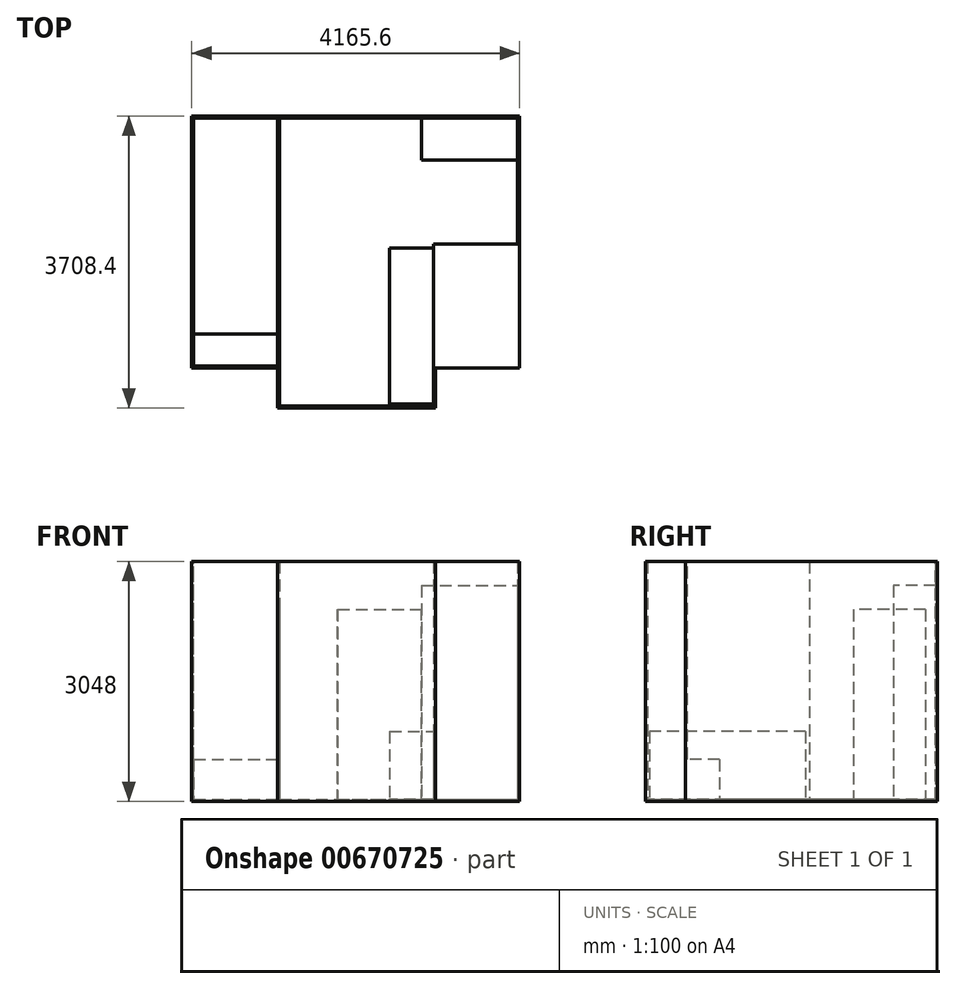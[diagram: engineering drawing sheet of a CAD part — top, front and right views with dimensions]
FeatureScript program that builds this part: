
annotation { "Feature Type Name" : "Feature", "Feature Type Description" : "" }
export const myFeature = defineFeature(function(context is Context, id is Id, definition is map)
    precondition{}
    {
        {
            var Q0;
            Q0=qCreatedBy(makeId("Top.planeOp"),FACE);
            var sketch = newSketch(context, id + "F0", { "sketchPlane" : qUnion([Q0])});
            skLineSegment(sketch, "E0.bottom", {"start": v(0, 0) * mm, "end": v(4165.6, 0) * mm});
            skLineSegment(sketch, "E0.top", {"start": v(1092.2, -3708.4) * mm, "end": v(3098.8, -3708.4) * mm});
            skLineSegment(sketch, "E0.left", {"start": v(0, 0) * mm, "end": v(0, -3200.4) * mm});
            skLineSegment(sketch, "E0.right", {"start": v(4165.6, 0) * mm, "end": v(4165.6, -3200.4) * mm});
            skLineSegment(sketch, "E1", {"start": v(0, -3200.4) * mm, "end": v(1092.2, -3200.4) * mm});
            skLineSegment(sketch, "E2", {"start": v(1092.2, -3200.4) * mm, "end": v(1092.2, -3708.4) * mm});
            skLineSegment(sketch, "E3", {"start": v(4165.6, -3200.4) * mm, "end": v(3098.8, -3200.4) * mm});
            skLineSegment(sketch, "E4", {"start": v(3098.8, -3200.4) * mm, "end": v(3098.8, -3708.4) * mm});
            skSolve(sketch);
        }
        {
            var Q0;
            Q0=makeQuery(id+"F0.imprint","IMPRINT",FACE,{"disambiguationData":[TD([[makeQuery(id+"F0.imprint","IMPRINT",EDGE,{"derivedFrom":sQuery(id+"F0.wireOp",EDGE,"E0.bottom")}),-1.0]])]});
            var sketch = newSketch(context, id + "F1", { "sketchPlane" : qUnion([Q0])});
            skLineSegment(sketch, "E5.bottom", {"start": v(0, -3200.4) * mm, "end": v(1117.6, -3200.4) * mm});
            skLineSegment(sketch, "E5.top", {"start": v(0, 0) * mm, "end": v(1117.6, 0) * mm});
            skLineSegment(sketch, "E5.left", {"start": v(0, -3200.4) * mm, "end": v(0, 0) * mm});
            skLineSegment(sketch, "E6", {"start": v(1117.6, 0) * mm, "end": v(1117.6, -3200.4) * mm});
            skSolve(sketch);
        }
        {
            var Q0;
            Q0=makeQuery(id+"F0.imprint","IMPRINT",FACE,{"disambiguationData":[TD([[makeQuery(id+"F0.imprint","IMPRINT",EDGE,{"derivedFrom":sQuery(id+"F0.wireOp",EDGE,"E0.bottom")}),-1.0]])]});
            var sketch = newSketch(context, id + "F2", { "sketchPlane" : qUnion([Q0])});
            skLineSegment(sketch, "E7.bottom", {"start": v(4165.6, -3200.4) * mm, "end": v(3073.4, -3200.4) * mm});
            skLineSegment(sketch, "E7.top", {"start": v(4165.6, -1625.6) * mm, "end": v(3073.4, -1625.6) * mm});
            skLineSegment(sketch, "E7.left", {"start": v(4165.6, -3200.4) * mm, "end": v(4165.6, -1625.6) * mm});
            skLineSegment(sketch, "E7.right", {"start": v(3073.4, -3200.4) * mm, "end": v(3073.4, -1625.6) * mm});
            skSolve(sketch);
        }
        {
            var Q0;
            Q0=makeQuery(id+"F0.imprint","IMPRINT",FACE,{"disambiguationData":[TD([[makeQuery(id+"F0.imprint","IMPRINT",EDGE,{"derivedFrom":sQuery(id+"F0.wireOp",EDGE,"E0.bottom")}),-1.0]])]});
            var sketch = newSketch(context, id + "F3", { "sketchPlane" : qUnion([Q0])});
            skLineSegment(sketch, "E8.bottom", {"start": v(4165.6, 0) * mm, "end": v(2921, 0) * mm});
            skLineSegment(sketch, "E8.top", {"start": v(4165.6, -558.8) * mm, "end": v(2921, -558.8) * mm});
            skLineSegment(sketch, "E8.left", {"start": v(4165.6, 0) * mm, "end": v(4165.6, -558.8) * mm});
            skLineSegment(sketch, "E8.right", {"start": v(2921, 0) * mm, "end": v(2921, -558.8) * mm});
            skSolve(sketch);
        }
        {
            var Q0;
            Q0=qCreatedBy(makeId("Top.planeOp"),FACE);
            var sketch = newSketch(context, id + "F4", { "sketchPlane" : qUnion([Q0])});
            skLineSegment(sketch, "E9.bottom", {"start": v(2514.6, -1676.4) * mm, "end": v(3073.4, -1676.4) * mm});
            skLineSegment(sketch, "E9.top", {"start": v(2514.6, -3657.6) * mm, "end": v(3073.4, -3657.6) * mm});
            skLineSegment(sketch, "E9.left", {"start": v(2514.6, -1676.4) * mm, "end": v(2514.6, -3657.6) * mm});
            skLineSegment(sketch, "E9.right", {"start": v(3073.4, -1676.4) * mm, "end": v(3073.4, -3657.6) * mm});
            skSolve(sketch);
        }
        {
            var Q0;
            Q0 = qSketchRegion(id + "F0", true);
            extrude(context, id + "F5", {"entities" : qUnion([Q0]), "depth" : 3048 * mm, "offsetDistance" : 25.4 * mm});
        }
        {
            var Q0;
            Q0=makeQuery(id+"F5.opExtrude","SWEPT_FACE",FACE,{"disambiguationData":[OSD([sQuery(id+"F0.wireOp",EDGE,"E0.bottom")])]});
            var sketch = newSketch(context, id + "F6", { "sketchPlane" : qUnion([Q0])});
            skLineSegment(sketch, "E10.bottom", {"start": v(-2921, 0) * mm, "end": v(-1854.2, 0) * mm});
            skLineSegment(sketch, "E10.top", {"start": v(-2921, 2438.4) * mm, "end": v(-1854.2, 2438.4) * mm});
            skLineSegment(sketch, "E10.left", {"start": v(-2921, 0) * mm, "end": v(-2921, 2438.4) * mm});
            skLineSegment(sketch, "E10.right", {"start": v(-1854.2, 0) * mm, "end": v(-1854.2, 2438.4) * mm});
            skSolve(sketch);
        }
        {
            var Q0;
            Q0=makeQuery(id+"F5.opExtrude","CAP_FACE",FACE,{"disambiguationData":[OSD([sQuery(id+"F0.wireOp",EDGE,"E0.bottom"),sQuery(id+"F0.wireOp",EDGE,"E0.top"),sQuery(id+"F0.wireOp",EDGE,"E0.left"),sQuery(id+"F0.wireOp",EDGE,"E0.right"),sQuery(id+"F0.wireOp",EDGE,"E1"),sQuery(id+"F0.wireOp",EDGE,"E2"),sQuery(id+"F0.wireOp",EDGE,"E3"),sQuery(id+"F0.wireOp",EDGE,"E4")])],"isStart":false});
            shell(context, id + "F7", {"entities" : qUnion([Q0]), "thickness" : 25.4 * mm});
        }
        {
            var Q0;
            Q0=makeQuery(id+"F6.imprint","IMPRINT",FACE,{"disambiguationData":[TD([[makeQuery(id+"F6.imprint","IMPRINT",EDGE,{"derivedFrom":sQuery(id+"F6.wireOp",EDGE,"E10.bottom")}),-1.0]])]});
            var Q1;
            Q1=makeQuery(id+"F7.opShell","OFFSET_FACE",FACE,{"disambiguationData":[OSD([sQuery(id+"F0.wireOp",EDGE,"E0.bottom")])]});
            extrude(context, id + "F8", {"entities" : qUnion([Q0]), "operationType" : NewBodyOperationType.REMOVE, "endBound" : BoundingType.UP_TO_SURFACE, "oppositeDirection" : true, "depth" : 25.4 * mm, "endBoundEntityFace" : qUnion([Q1]), "offsetDistance" : 25.4 * mm});
        }
        {
            var Q0;
            Q0 = qSketchRegion(id + "F1", true);
            extrude(context, id + "F9", {"entities" : qUnion([Q0]), "operationType" : NewBodyOperationType.ADD, "depth" : 3048 * mm, "offsetDistance" : 25.4 * mm});
        }
        {
            var Q0;
            Q0 = qSketchRegion(id + "F2", true);
            extrude(context, id + "F10", {"entities" : qUnion([Q0]), "operationType" : NewBodyOperationType.ADD, "depth" : 3048 * mm, "offsetDistance" : 25.4 * mm});
        }
        {
            var Q0;
            Q0 = qSketchRegion(id + "F4", true);
            extrude(context, id + "F11", {"entities" : qUnion([Q0]), "operationType" : NewBodyOperationType.ADD, "depth" : 889 * mm, "offsetDistance" : 25.4 * mm});
        }
        {
            var Q0;
            Q0 = qSketchRegion(id + "F3", true);
            extrude(context, id + "F12", {"entities" : qUnion([Q0]), "operationType" : NewBodyOperationType.ADD, "depth" : 508 * mm, "offsetDistance" : 25.4 * mm});
        }
        {
            var Q0;
            {var subQ0=sQuery(id+"F3.wireOp",EDGE,"E8.top");var subQ1=sQuery(id+"F3.wireOp",EDGE,"E8.right");Q0=makeQuery(id+"F12.boolean.opBoolean","SPLIT",FACE,{"disambiguationData":[TD([makeQuery(id+"F7.opShell","OFFSET_FACE",FACE,{"disambiguationData":[OSD([sQuery(id+"F0.wireOp",EDGE,"E0.bottom")])]})])],"derivedFrom":makeQuery(id+"F12.opExtrude","CAP_FACE",FACE,{"disambiguationData":[OSD([sQuery(id+"F3.wireOp",EDGE,"E8.bottom"),subQ0,sQuery(id+"F3.wireOp",EDGE,"E8.left"),subQ1])],"isStart":false})});}
            var sketch = newSketch(context, id + "F13", { "sketchPlane" : qUnion([Q0])});
            skLineSegment(sketch, "E11.bottom", {"start": v(4140.2, -558.8) * mm, "end": v(2921, -558.8) * mm});
            skLineSegment(sketch, "E11.top", {"start": v(4140.2, -25.4) * mm, "end": v(2921, -25.4) * mm});
            skLineSegment(sketch, "E11.left", {"start": v(4140.2, -558.8) * mm, "end": v(4140.2, -25.4) * mm});
            skLineSegment(sketch, "E11.right", {"start": v(2921, -558.8) * mm, "end": v(2921, -25.4) * mm});
            skSolve(sketch);
        }
        {
            var Q0;
            Q0 = qSketchRegion(id + "F13", true);
            extrude(context, id + "F14", {"entities" : qUnion([Q0]), "operationType" : NewBodyOperationType.ADD, "depth" : 2235.2 * mm, "offsetDistance" : 25.4 * mm});
        }
        {
            var Q0;
            Q0=makeQuery(id+"F9.boolean.opBoolean","MERGE",FACE,{"derivedFrom":[makeQuery(id+"F7.opShell","OFFSET_FACE",FACE,{"disambiguationData":[OSD([sQuery(id+"F0.wireOp",EDGE,"E2")])]}),makeQuery(id+"F9.opExtrude","SWEPT_FACE",FACE,{"disambiguationData":[OSD([sQuery(id+"F1.wireOp",EDGE,"E6")])]})]});
            var sketch = newSketch(context, id + "F15", { "sketchPlane" : qUnion([Q0])});
            skLineSegment(sketch, "E12.bottom", {"start": v(-152.4, 2438.4) * mm, "end": v(-1066.8, 2438.4) * mm});
            skLineSegment(sketch, "E12.top", {"start": v(-152.4, 0) * mm, "end": v(-1066.8, 0) * mm});
            skLineSegment(sketch, "E12.left", {"start": v(-152.4, 2438.4) * mm, "end": v(-152.4, 0) * mm});
            skLineSegment(sketch, "E12.right", {"start": v(-1066.8, 2438.4) * mm, "end": v(-1066.8, 0) * mm});
            skSolve(sketch);
        }
        {
            var Q0;
            Q0=makeQuery(id+"F10.boolean.opBoolean","MERGE",FACE,{"derivedFrom":[makeQuery(id+"F9.boolean.opBoolean","MERGE",FACE,{"derivedFrom":[makeQuery(id+"F5.opExtrude","CAP_FACE",FACE,{"disambiguationData":[OSD([sQuery(id+"F0.wireOp",EDGE,"E0.bottom"),sQuery(id+"F0.wireOp",EDGE,"E0.top"),sQuery(id+"F0.wireOp",EDGE,"E0.left"),sQuery(id+"F0.wireOp",EDGE,"E0.right"),sQuery(id+"F0.wireOp",EDGE,"E1"),sQuery(id+"F0.wireOp",EDGE,"E2"),sQuery(id+"F0.wireOp",EDGE,"E3"),sQuery(id+"F0.wireOp",EDGE,"E4")])],"isStart":false}),makeQuery(id+"F9.opExtrude","CAP_FACE",FACE,{"disambiguationData":[OSD([sQuery(id+"F1.wireOp",EDGE,"E5.bottom"),sQuery(id+"F1.wireOp",EDGE,"E5.top"),sQuery(id+"F1.wireOp",EDGE,"E5.left"),sQuery(id+"F1.wireOp",EDGE,"E6")])],"isStart":false})]}),makeQuery(id+"F10.opExtrude","CAP_FACE",FACE,{"disambiguationData":[OSD([sQuery(id+"F2.wireOp",EDGE,"E7.bottom"),sQuery(id+"F2.wireOp",EDGE,"E7.top"),sQuery(id+"F2.wireOp",EDGE,"E7.left"),sQuery(id+"F2.wireOp",EDGE,"E7.right")])],"isStart":false})]});
            var sketch = newSketch(context, id + "F16", { "sketchPlane" : qUnion([Q0])});
            skLineSegment(sketch, "E13.bottom", {"start": v(25.4, -25.4) * mm, "end": v(1092.2, -25.4) * mm});
            skLineSegment(sketch, "E13.top", {"start": v(25.4, -3175) * mm, "end": v(1092.2, -3175) * mm});
            skLineSegment(sketch, "E13.left", {"start": v(25.4, -25.4) * mm, "end": v(25.4, -3175) * mm});
            skLineSegment(sketch, "E13.right", {"start": v(1092.2, -25.4) * mm, "end": v(1092.2, -3175) * mm});
            skSolve(sketch);
        }
        {
            var Q0;
            Q0=makeQuery(id+"F16.imprint","IMPRINT",FACE,{"disambiguationData":[TD([[makeQuery(id+"F16.imprint","IMPRINT",EDGE,{"derivedFrom":sQuery(id+"F16.wireOp",EDGE,"E13.bottom")}),-1.0]])]});
            extrude(context, id + "F17", {"entities" : qUnion([Q0]), "operationType" : NewBodyOperationType.REMOVE, "oppositeDirection" : true, "depth" : 3022.6 * mm, "offsetDistance" : 25.4 * mm});
        }
        {
            var Q0;
            {var subQ0=sQuery(id+"F15.wireOp",EDGE,"E12.bottom");Q0=makeQuery(id+"F15.imprint","IMPRINT",FACE,{"disambiguationData":[TD([[makeQuery(id+"F15.imprint","IMPRINT",EDGE,{"derivedFrom":subQ0}),1.0]])]});}
            extrude(context, id + "F18", {"entities" : qUnion([Q0]), "operationType" : NewBodyOperationType.REMOVE, "oppositeDirection" : true, "depth" : 25.4 * mm, "offsetDistance" : 25.4 * mm});
        }
        {
            var Q0;
            {var subQ0=sQuery(id+"F0.wireOp",EDGE,"E4");var subQ1=sQuery(id+"F0.wireOp",EDGE,"E3");var subQ2=sQuery(id+"F0.wireOp",EDGE,"E2");var subQ3=sQuery(id+"F0.wireOp",EDGE,"E1");var subQ4=sQuery(id+"F0.wireOp",EDGE,"E0.right");var subQ5=sQuery(id+"F0.wireOp",EDGE,"E0.left");var subQ6=sQuery(id+"F0.wireOp",EDGE,"E0.top");var subQ7=sQuery(id+"F0.wireOp",EDGE,"E0.bottom");Q0=makeQuery(id+"F18.boolean.opBoolean","MERGE",FACE,{"derivedFrom":[makeQuery(id+"F7.opShell","OFFSET_FACE",FACE,{"disambiguationData":[OSD([subQ7,subQ6,subQ5,subQ4,subQ3,subQ2,subQ1,subQ0])]}),makeQuery(id+"F17.boolean.opBoolean","COPY",FACE,{"derivedFrom":makeQuery(id+"F17.opExtrude","CAP_FACE",FACE,{"disambiguationData":[OSD([sQuery(id+"F16.wireOp",EDGE,"E13.bottom"),sQuery(id+"F16.wireOp",EDGE,"E13.top"),sQuery(id+"F16.wireOp",EDGE,"E13.left"),sQuery(id+"F16.wireOp",EDGE,"E13.right")])],"isStart":false})})],"fromTools":[makeQuery(id+"F18.opExtrude","SWEPT_FACE",FACE,{"disambiguationData":[OSD([subQ7,subQ6,subQ5,subQ4,subQ3,subQ2,subQ1,subQ0,sQuery(id+"F1.wireOp",EDGE,"E6")])]})]});}
            var sketch = newSketch(context, id + "F19", { "sketchPlane" : qUnion([Q0])});
            skLineSegment(sketch, "E14.bottom", {"start": v(25.4, -2768.6) * mm, "end": v(1092.2, -2768.6) * mm});
            skLineSegment(sketch, "E14.top", {"start": v(25.4, -3175) * mm, "end": v(1092.2, -3175) * mm});
            skLineSegment(sketch, "E14.left", {"start": v(25.4, -2768.6) * mm, "end": v(25.4, -3175) * mm});
            skLineSegment(sketch, "E14.right", {"start": v(1092.2, -2768.6) * mm, "end": v(1092.2, -3175) * mm});
            skSolve(sketch);
        }
        {
            var Q0;
            Q0=makeQuery(id+"F19.imprint","IMPRINT",FACE,{"disambiguationData":[TD([[makeQuery(id+"F19.imprint","IMPRINT",EDGE,{"derivedFrom":sQuery(id+"F19.wireOp",EDGE,"E14.bottom")}),-1.0]])]});
            extrude(context, id + "F20", {"entities" : qUnion([Q0]), "operationType" : NewBodyOperationType.ADD, "depth" : 508 * mm, "offsetDistance" : 25.4 * mm});
        }
    });
